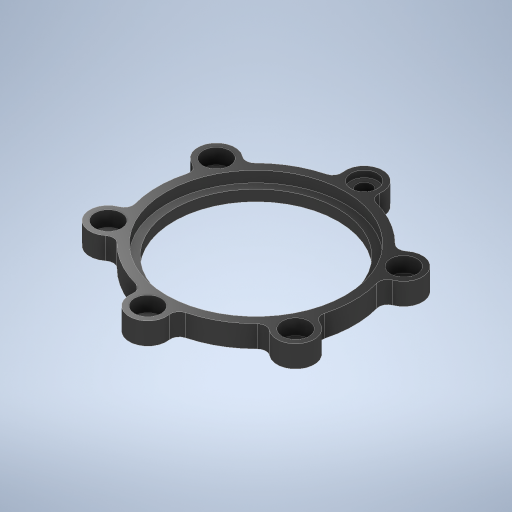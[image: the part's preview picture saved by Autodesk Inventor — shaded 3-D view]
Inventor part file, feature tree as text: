
AUTODESK INVENTOR PART (.ipt)
format: ipt  version: 2024.2 (Build 282272000, 272)  size: 343,552 bytes
history: native  units: mm
features: hole x3, sketch x1, extrude x1, fillet x1
ambient origin geometry x8: Origin, YZ Plane, XZ Plane, XY Plane, X Axis, Y Axis, Z Axis, Center Point
bodies: Solid1 (feature_tree)
feature tree (6):
  sketch  "Sketch1"  dims[d0=0.0mm d13=6.0mm d16=90.0deg d17=6.0mm d18=0.0mm d21=6.0mm d24=90.0deg d25=8.0mm d26=0.0mm d31=3.5mm d32=6.0mm d33=6.1mm d34=1.5mm d35=90.0deg d36=8.0mm d37=0.0mm d38=2.0mm d39=60.0mm d41=360.0deg]
  extrude  "Extrusion1"  Depth=2.0mm
  hole  "Hole1"  [1 undecoded]
  hole  "Hole2"  [1 undecoded]
  hole  "Hole3"  [1 undecoded]
  fillet  "Fillet1"  Radius=3.5mm
note: 3 required parameter values undecoded (feature->parameter linkage not recoverable at this tier; creation-order binding heuristic only, values carry confidence <= 0.55)
